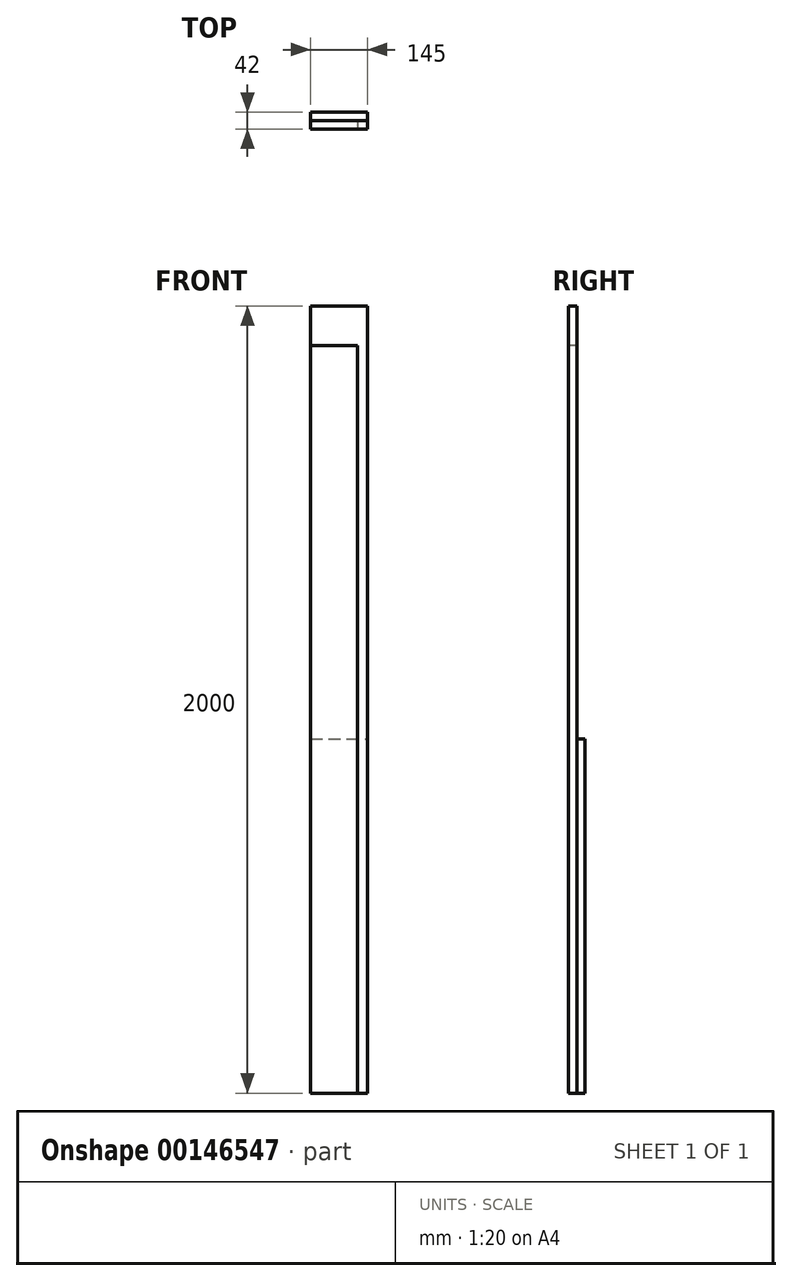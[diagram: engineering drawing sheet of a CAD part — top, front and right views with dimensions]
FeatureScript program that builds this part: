
annotation { "Feature Type Name" : "Feature", "Feature Type Description" : "" }
export const myFeature = defineFeature(function(context is Context, id is Id, definition is map)
    precondition{}
    {
        {
            var Q0;
            Q0=qCreatedBy(makeId("Top.planeOp"),FACE);
            var sketch = newSketch(context, id + "F0", { "sketchPlane" : qUnion([Q0])});
            skLineSegment(sketch, "E0.bottom", {"start": v(0, 0) * mm, "end": v(120, 0) * mm});
            skLineSegment(sketch, "E0.top", {"start": v(0, -21) * mm, "end": v(120, -21) * mm});
            skLineSegment(sketch, "E0.left", {"start": v(0, 0) * mm, "end": v(0, -21) * mm});
            skLineSegment(sketch, "E0.right", {"start": v(120, 0) * mm, "end": v(120, -21) * mm});
            skSolve(sketch);
        }
        {
            assignVariable(context, id + "F1", {"name" : "height", "anyValue" : 1900});
        }
        {
            var Q0;
            Q0=makeQuery(id+"F0.imprint","IMPRINT",FACE,{"disambiguationData":[TD([[makeQuery(id+"F0.imprint","IMPRINT",EDGE,{"derivedFrom":sQuery(id+"F0.wireOp",EDGE,"E0.bottom")}),-1.0]])]});
            extrude(context, id + "F2", {"entities" : qUnion([Q0]), "depth" : (getVariable(context, 'height')) * mm});
        }
        {
            var Q0;
            Q0=qCreatedBy(makeId("Top.planeOp"),FACE);
            var sketch = newSketch(context, id + "F3", { "sketchPlane" : qUnion([Q0])});
            skLineSegment(sketch, "E1.bottom", {"start": v(0, 0) * mm, "end": v(145, 0) * mm});
            skLineSegment(sketch, "E1.top", {"start": v(0, 21) * mm, "end": v(145, 21) * mm});
            skLineSegment(sketch, "E1.left", {"start": v(0, 0) * mm, "end": v(0, 21) * mm});
            skLineSegment(sketch, "E1.right", {"start": v(145, 0) * mm, "end": v(145, 21) * mm});
            skSolve(sketch);
        }
        {
            var Q0;
            Q0 = qSketchRegion(id + "F3", true);
            extrude(context, id + "F4", {"entities" : qUnion([Q0]), "depth" : (120 * 7 + 10 * 6) * mm});
        }
        {
            var Q0;
            Q0=qCreatedBy(makeId("Top.planeOp"),FACE);
            var sketch = newSketch(context, id + "F5", { "sketchPlane" : qUnion([Q0])});
            skLineSegment(sketch, "E2.bottom", {"start": v(0, 0) * mm, "end": v(145, 0) * mm});
            skLineSegment(sketch, "E2.top", {"start": v(0, -21) * mm, "end": v(145, -21) * mm});
            skLineSegment(sketch, "E2.left", {"start": v(0, 0) * mm, "end": v(0, -21) * mm});
            skLineSegment(sketch, "E2.right", {"start": v(145, 0) * mm, "end": v(145, -21) * mm});
            skSolve(sketch);
        }
        {
            var Q0;
            Q0 = qSketchRegion(id + "F5", true);
            extrude(context, id + "F6", {"entities" : qUnion([Q0]), "depth" : 2000 * mm});
        }
    });
